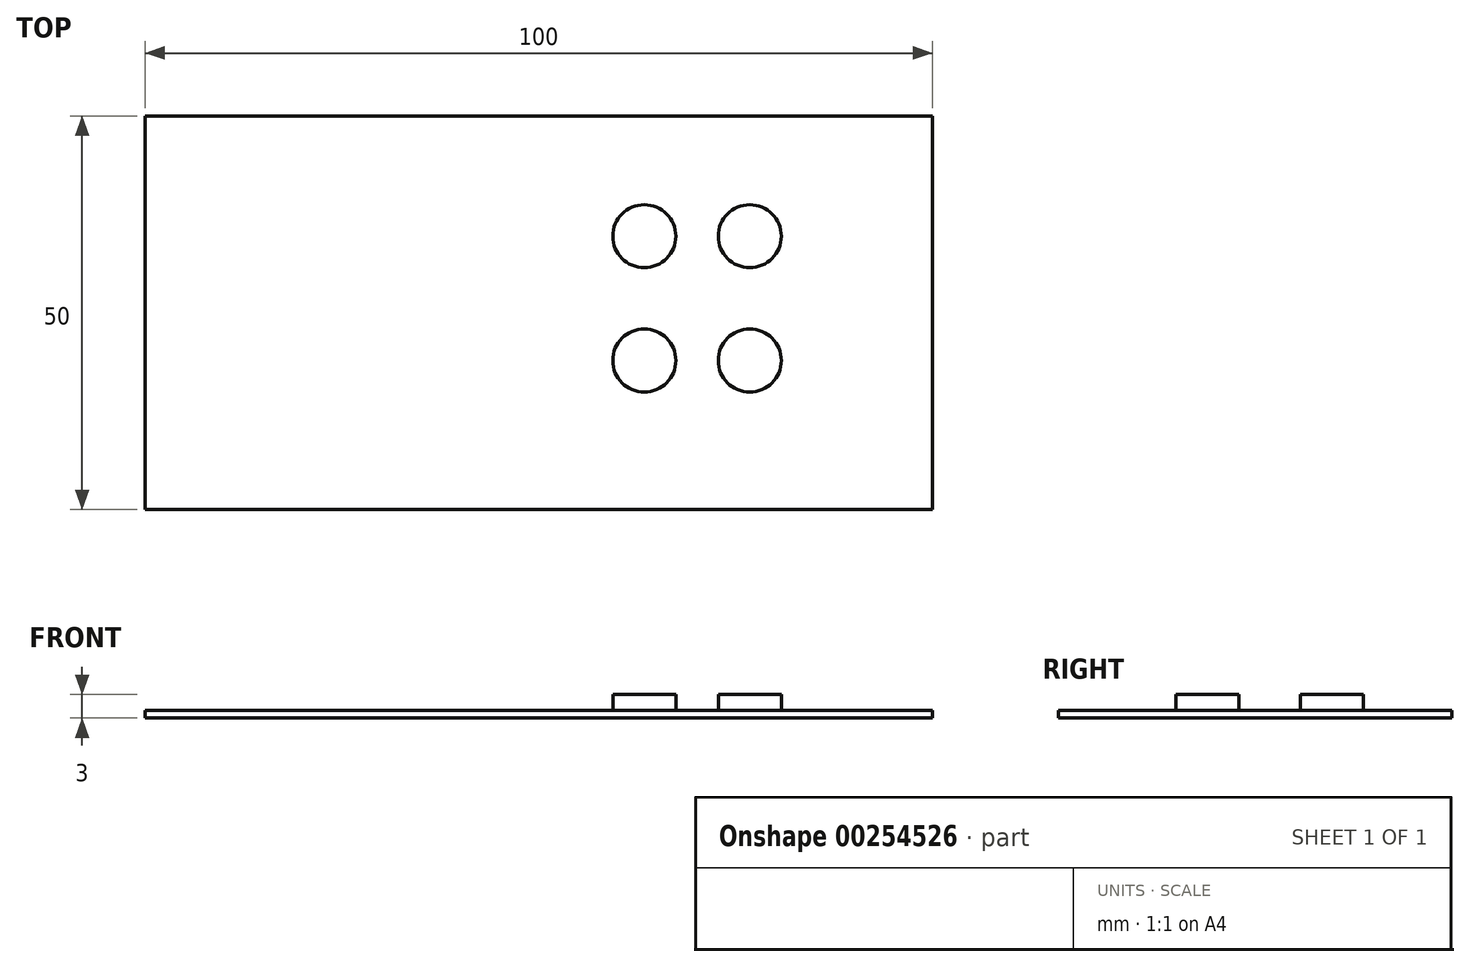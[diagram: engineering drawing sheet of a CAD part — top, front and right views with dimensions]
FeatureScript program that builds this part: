
annotation { "Feature Type Name" : "Feature", "Feature Type Description" : "" }
export const myFeature = defineFeature(function(context is Context, id is Id, definition is map)
    precondition{}
    {
        {
            var Q0;
            Q0=qCreatedBy(makeId("Top.planeOp"),FACE);
            var sketch = newSketch(context, id + "F0", { "sketchPlane" : qUnion([Q0])});
            skLineSegment(sketch, "E0.bottom", {"start": v(50, 25) * mm, "end": v(-50, 25) * mm});
            skLineSegment(sketch, "E0.top", {"start": v(50, -25) * mm, "end": v(-50, -25) * mm});
            skLineSegment(sketch, "E0.left", {"start": v(50, 25) * mm, "end": v(50, -25) * mm});
            skLineSegment(sketch, "E0.right", {"start": v(-50, 25) * mm, "end": v(-50, -25) * mm});
            skPoint(sketch, "E0.middle", {"position": v(0, 0) * mm});
            skSolve(sketch);
        }
        {
            var Q0;
            Q0=makeQuery(id+"F0.imprint","IMPRINT",FACE,{"disambiguationData":[TD([[makeQuery(id+"F0.imprint","IMPRINT",EDGE,{"derivedFrom":sQuery(id+"F0.wireOp",EDGE,"E0.bottom")}),1.0]])]});
            extrude(context, id + "F1", {"entities" : qUnion([Q0]), "depth" : 3 * mm, "offsetDistance" : 25 * mm});
        }
        {
            var Q0;
            Q0=makeQuery(id+"F1.opExtrude","CAP_FACE",FACE,{"disambiguationData":[OSD([sQuery(id+"F0.wireOp",EDGE,"E0.bottom"),sQuery(id+"F0.wireOp",EDGE,"E0.top"),sQuery(id+"F0.wireOp",EDGE,"E0.left"),sQuery(id+"F0.wireOp",EDGE,"E0.right")])],"isStart":false});
            var sketch = newSketch(context, id + "F2", { "sketchPlane" : qUnion([Q0])});
            skCircle(sketch, "E1", {"center": v(0, 9.72) * mm, "radius": 4 * mm});
            skCircle(sketch, "E2.0.1.0", {"center": v(0, -6.08) * mm, "radius": 4 * mm});
            skCircle(sketch, "E2.1.0.0", {"center": v(-13.4, 9.72) * mm, "radius": 4 * mm});
            skCircle(sketch, "E2.1.1.0", {"center": v(-13.4, -6.08) * mm, "radius": 4 * mm});
            skCircle(sketch, "E2.2.0.0", {"center": v(-26.8, 9.72) * mm, "radius": 4 * mm});
            skCircle(sketch, "E2.2.1.0", {"center": v(-26.8, -6.08) * mm, "radius": 4 * mm});
            skLineSegment(sketch, "E2.direction1", {"start": v(0, 9.72) * mm, "end": v(-13.4, 9.72) * mm, "construction": true});
            skLineSegment(sketch, "E2.direction2", {"start": v(0, 9.72) * mm, "end": v(0, -6.08) * mm, "construction": true});
            skCircle(sketch, "E3.MirrorC", {"center": v(13.4, 9.72) * mm, "radius": 4 * mm});
            skCircle(sketch, "E4.MirrorC", {"center": v(13.4, -6.08) * mm, "radius": 4 * mm});
            skCircle(sketch, "E5.MirrorC", {"center": v(26.8, -6.08) * mm, "radius": 4 * mm});
            skCircle(sketch, "E6.MirrorC", {"center": v(26.8, 9.72) * mm, "radius": 4 * mm});
            skSolve(sketch);
        }
        {
            var Q0;
            Q0=makeQuery(id+"F2.imprint","IMPRINT",FACE,{"disambiguationData":[TD([[makeQuery(id+"F2.imprint","IMPRINT",EDGE,{"derivedFrom":sQuery(id+"F2.wireOp",EDGE,"E2.2.0.0")}),1.0]])]});
            var Q1;
            Q1=makeQuery(id+"F2.imprint","IMPRINT",FACE,{"disambiguationData":[TD([[makeQuery(id+"F2.imprint","IMPRINT",EDGE,{"derivedFrom":sQuery(id+"F2.wireOp",EDGE,"E2.2.1.0")}),1.0]])]});
            var Q2;
            Q2=makeQuery(id+"F2.imprint","IMPRINT",FACE,{"disambiguationData":[TD([[makeQuery(id+"F2.imprint","IMPRINT",EDGE,{"derivedFrom":sQuery(id+"F2.wireOp",EDGE,"E2.1.1.0")}),1.0]])]});
            var Q3;
            Q3=makeQuery(id+"F2.imprint","IMPRINT",FACE,{"disambiguationData":[TD([[makeQuery(id+"F2.imprint","IMPRINT",EDGE,{"derivedFrom":sQuery(id+"F2.wireOp",EDGE,"E2.1.0.0")}),1.0]])]});
            var Q4;
            Q4=makeQuery(id+"F2.imprint","IMPRINT",FACE,{"disambiguationData":[TD([[makeQuery(id+"F2.imprint","IMPRINT",EDGE,{"derivedFrom":sQuery(id+"F2.wireOp",EDGE,"E1")}),1.0]])]});
            var Q5;
            Q5=makeQuery(id+"F2.imprint","IMPRINT",FACE,{"disambiguationData":[TD([[makeQuery(id+"F2.imprint","IMPRINT",EDGE,{"derivedFrom":sQuery(id+"F2.wireOp",EDGE,"E2.0.1.0")}),1.0]])]});
            var Q6;
            Q6=makeQuery(id+"F2.imprint","IMPRINT",FACE,{"disambiguationData":[TD([[makeQuery(id+"F2.imprint","IMPRINT",EDGE,{"derivedFrom":sQuery(id+"F2.wireOp",EDGE,"E4.MirrorC")}),-1.0]])]});
            var Q7;
            Q7=makeQuery(id+"F2.imprint","IMPRINT",FACE,{"disambiguationData":[TD([[makeQuery(id+"F2.imprint","IMPRINT",EDGE,{"derivedFrom":sQuery(id+"F2.wireOp",EDGE,"E3.MirrorC")}),-1.0]])]});
            var Q8;
            Q8=makeQuery(id+"F2.imprint","IMPRINT",FACE,{"disambiguationData":[TD([[makeQuery(id+"F2.imprint","IMPRINT",EDGE,{"derivedFrom":sQuery(id+"F2.wireOp",EDGE,"E5.MirrorC")}),-1.0]])]});
            var Q9;
            Q9=makeQuery(id+"F2.imprint","IMPRINT",FACE,{"disambiguationData":[TD([[makeQuery(id+"F2.imprint","IMPRINT",EDGE,{"derivedFrom":sQuery(id+"F2.wireOp",EDGE,"E6.MirrorC")}),-1.0]])]});
            extrude(context, id + "F3", {"entities" : qUnion([Q0, Q1, Q2, Q3, Q4, Q5, Q6, Q7, Q8, Q9]), "operationType" : NewBodyOperationType.REMOVE, "oppositeDirection" : true, "depth" : 2 * mm, "offsetDistance" : 25 * mm});
        }
    });
